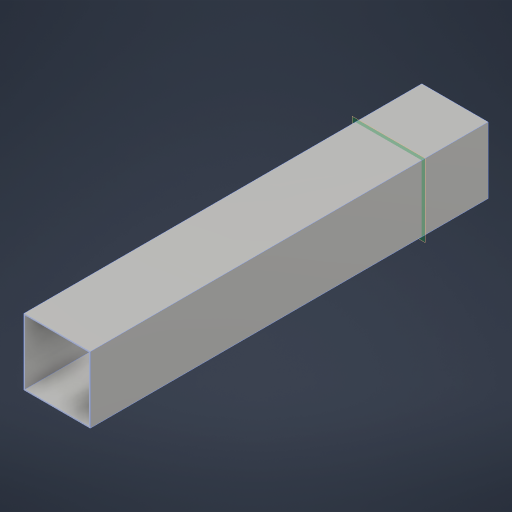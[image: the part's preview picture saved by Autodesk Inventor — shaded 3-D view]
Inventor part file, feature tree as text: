
AUTODESK INVENTOR PART (.ipt)
format: ipt  version: 2024.2 (Build 282272000, 272)  size: 172,032 bytes
history: native  units: in
note: dims shown in document units (in); Inventor stores cm internally (conversion verified against a paired STEP export)
features: extrude x1, plane x1
ambient origin geometry x8: Origin, YZ Plane, XZ Plane, XY Plane, X Axis, Y Axis, Z Axis, Center Point
bodies: Solid1 (feature_tree)
feature tree (2):
  extrude  "Extrusion1"  TaperAngle=0.0deg  [1 undecoded]
  plane  "Work Plane1"
note: 1 required parameter value undecoded (feature->parameter linkage not recoverable at this tier; creation-order binding heuristic only, values carry confidence <= 0.55)
